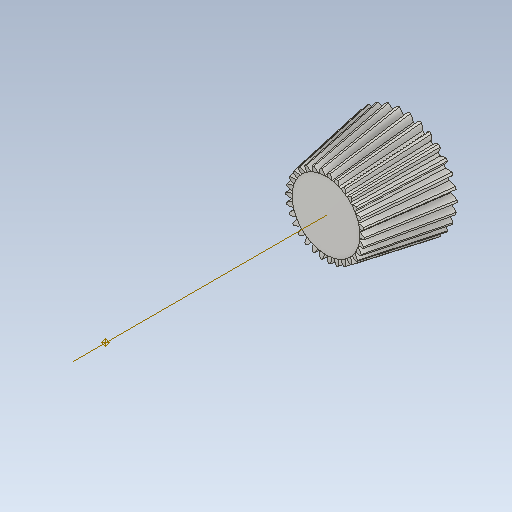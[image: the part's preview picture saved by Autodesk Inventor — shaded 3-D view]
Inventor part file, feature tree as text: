
AUTODESK INVENTOR PART (.ipt)
format: ipt  version: 2021 (Build 250183000, 183)  size: 667,136 bytes
history: native  units: mm
features: other x24, loft x2, pattern_circular x2, sketch x1
ambient origin geometry x6: Origin, XZ Plane, X Axis, Y Axis, Z Axis, Center Point
bodies: Solid1 (feature_tree)
feature tree (29):
  other  "Top Point"
  other  "Mesh Plane2"
  other  "Teeth Body"
  other  "Start Point"
  other  "Tooth Plane"
  other  "Start Sketch"
  other  "End Point"
  other  "3D Sketch Right"
  other  "End Plane Right"
  loft  "Loft Right"
  pattern_circular  "Circular Pattern Right"  [2 undecoded]
  other  "3D Sketch Left"
  other  "End Plane Left"
  loft  "Loft Left"
  pattern_circular  "Circular Pattern Left"  [2 undecoded]
  other  "Fix Body"
  other  "Mesh Plane"
  other  "Top Plane"
  other  "Teeth Body Sketch"
  other  "End Plane"
  other  "End Sketch"
  other  "Helical Curve Left"
  other  "End Sketch Left"
  other  "Body Sketch"
  sketch  "Sketch6"  dims[d0=31.75mm d1=29.244559mm d2=33.837867mm d3=25.4mm d4=95.076011mm d5=90.0deg d7=5.865417mm d8=6.223675mm d9=13.765897mm d11=25.516417mm d12=4.315516mm d15=4.579106mm d16=10.128341mm d17=0.0mm d18=90.0deg d19=0.0mm d20=90.0deg d21=300.0mm d22=360.0deg d26=234.767701mm d27=25.169238mm d28=31.75mm d29=-1.651487mm d30=4.315516mm d31=4.579106mm d32=10.128341mm d35=0.0mm d37=0.0mm d39=0.0mm d40=90.0deg d41=300.0mm d42=360.0deg d46=90.0deg d47=90.0deg d48=0.0mm d49=0.0mm d50=90.0deg d51=1.047198mm d52=0.0mm d53=0.0mm d54=0.0mm d56=12.299615mm d57=17.850809mm d58=14.544576mm d59=13.13384mm d60=10.701259mm d61=13.13384mm d62=10.701259mm d63=90.0deg d64=90.0deg d65=234.767701mm d66=31.5mm d67=31.75mm d68=-1.651487mm d69=25.169238mm d70=4.579106mm d71=10.128341mm d72=4.315516mm d73=10.701259mm d74=13.13384mm d75=0.0mm d76=90.0deg d77=0.0mm d78=90.0deg d79=0.0mm d80=90.0deg d81=300.0mm d82=360.0deg d84=10.0mm d85=20.0mm d86=20.0mm d87=10.0mm d88=0.0mm d89=0.0mm]
  other  "Srf1"
  other  "Helical Curve Right"
  other  "End Sketch Right"
  other  "Pitch Diameter"
note: 4 required parameter values undecoded (feature->parameter linkage not recoverable at this tier; creation-order binding heuristic only, values carry confidence <= 0.55)
